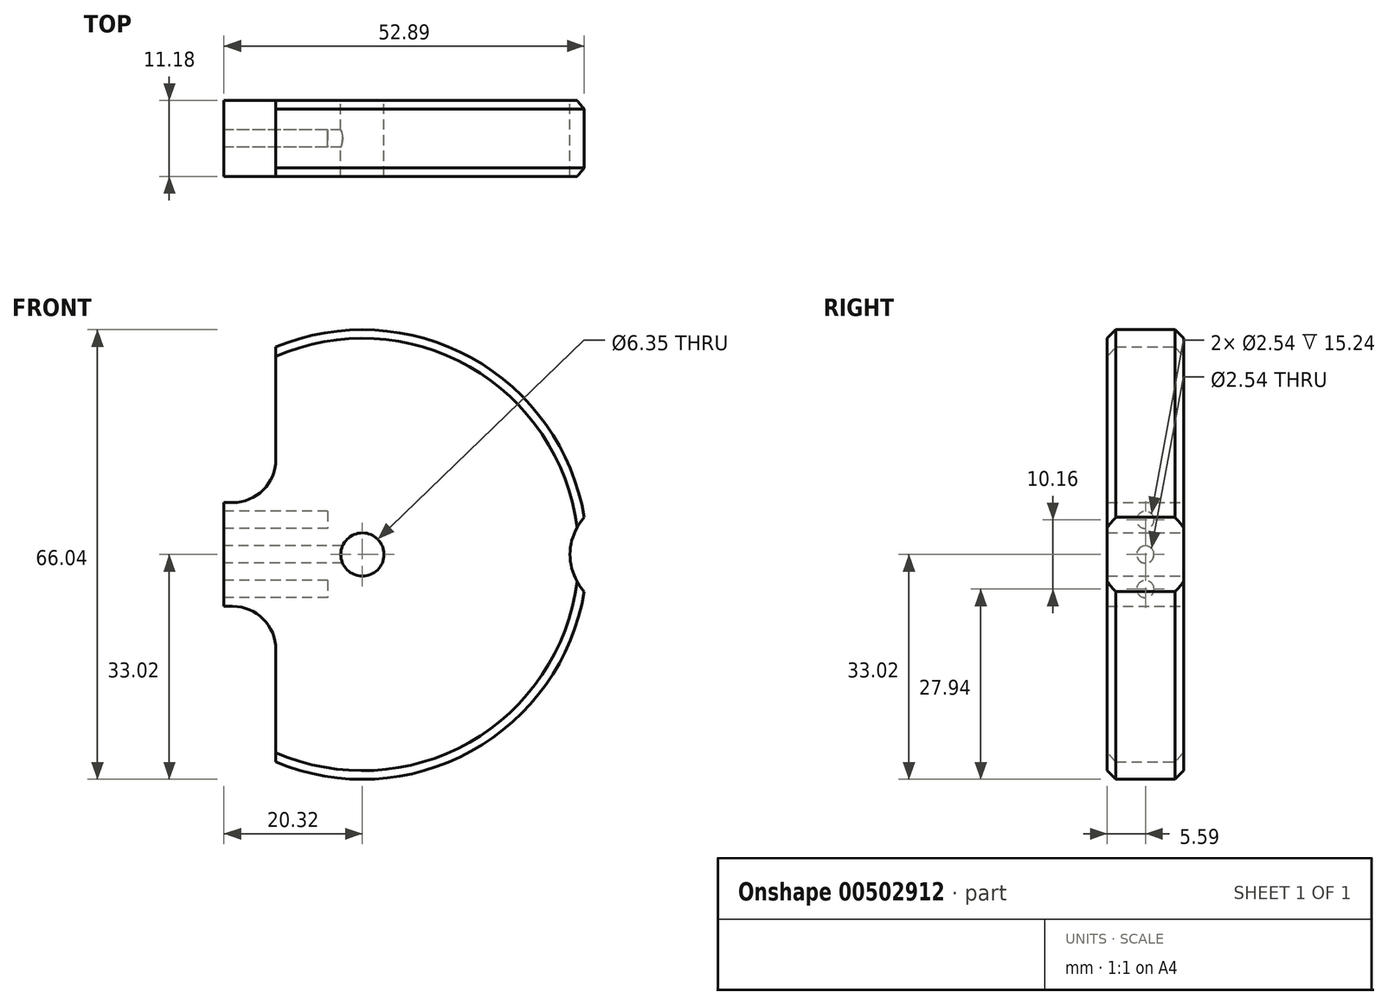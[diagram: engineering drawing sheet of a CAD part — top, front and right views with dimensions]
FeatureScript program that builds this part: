
annotation { "Feature Type Name" : "Feature", "Feature Type Description" : "" }
export const myFeature = defineFeature(function(context is Context, id is Id, definition is map)
    precondition{}
    {
        {
            var Q0;
            Q0=qCreatedBy(makeId("Front.planeOp"),FACE);
            var sketch = newSketch(context, id + "F0", { "sketchPlane" : qUnion([Q0])});
            skLineSegment(sketch, "E0", {"start": v(0, 0) * mm, "end": v(-82.35, 0) * mm, "construction": true});
            skLineSegment(sketch, "E1", {"start": v(-12.7, 30.48) * mm, "end": v(-12.7, 13.97) * mm});
            skLineSegment(sketch, "E2", {"start": v(-19.05, 7.62) * mm, "end": v(-20.32, 7.62) * mm});
            skLineSegment(sketch, "E3", {"start": v(-19.05, -7.62) * mm, "end": v(-20.32, -7.62) * mm});
            skLineSegment(sketch, "E4.trimOffspring", {"start": v(-20.32, 7.62) * mm, "end": v(-20.32, -7.62) * mm});
            skArc(sketch, "E5.trimOffspring", {"start": v(-12.7, -30.48) * mm, "mid": v(15.97, -28.9) * mm, "end": v(32.57, -5.46) * mm});
            skLineSegment(sketch, "E6.trimOffspring", {"start": v(-12.7, -13.97) * mm, "end": v(-12.7, -30.48) * mm});
            skCircle(sketch, "E7", {"center": v(0, 0) * mm, "radius": 3.18 * mm});
            skPoint(sketch, "E8.visualSharp", {"position": v(-12.7, 7.62) * mm});
            skArc(sketch, "E8.filletArc", {"start": v(-19.05, 7.62) * mm, "mid": v(-14.56, 9.48) * mm, "end": v(-12.7, 13.97) * mm});
            skPoint(sketch, "E9.visualSharp", {"position": v(-12.7, -7.62) * mm});
            skArc(sketch, "E9.filletArc", {"start": v(-12.7, -13.97) * mm, "mid": v(-14.56, -9.48) * mm, "end": v(-19.05, -7.62) * mm});
            skArc(sketch, "E10", {"start": v(32.57, 5.46) * mm, "mid": v(30.48, 0) * mm, "end": v(32.57, -5.46) * mm});
            skPoint(sketch, "E10.centerSnap0", {"position": v(33.02, 0) * mm});
            skArc(sketch, "E11.trimOffspring", {"start": v(32.57, 5.46) * mm, "mid": v(15.97, 28.9) * mm, "end": v(-12.7, 30.48) * mm});
            skSolve(sketch);
        }
        {
            var Q0;
            Q0 = qSketchRegion(id + "F0", true);
            extrude(context, id + "F1", {"entities" : qUnion([Q0]), "endBound" : BoundingType.SYMMETRIC, "depth" : 11.18 * mm});
        }
        {
            var Q0;
            Q0=makeQuery(id+"F1.opExtrude","SWEPT_FACE",FACE,{"disambiguationData":[OSD([sQuery(id+"F0.wireOp",EDGE,"E4.trimOffspring")])]});
            var sketch = newSketch(context, id + "F2", { "sketchPlane" : qUnion([Q0])});
            skCircle(sketch, "E12", {"center": v(0, 0) * mm, "radius": 1.27 * mm});
            skCircle(sketch, "E13", {"center": v(0, 5.08) * mm, "radius": 1.27 * mm});
            skCircle(sketch, "E14", {"center": v(0, -5.08) * mm, "radius": 1.27 * mm});
            skSolve(sketch);
        }
        {
            var Q0;
            Q0 = qSketchRegion(id + "F2", true);
            extrude(context, id + "F3", {"entities" : qUnion([Q0]), "operationType" : NewBodyOperationType.REMOVE, "oppositeDirection" : true, "depth" : 15.24 * mm});
        }
        {
            var Q0;
            Q0=makeQuery(id+"F2.imprint","IMPRINT",FACE,{"disambiguationData":[TD([[makeQuery(id+"F2.imprint","IMPRINT",EDGE,{"derivedFrom":sQuery(id+"F2.wireOp",EDGE,"E12")}),1.0]])]});
            extrude(context, id + "F4", {"entities" : qUnion([Q0]), "operationType" : NewBodyOperationType.REMOVE, "oppositeDirection" : true, "depth" : 19.05 * mm});
        }
        {
            var Q0;
            Q0=makeQuery(id+"F1.opExtrude","CAP_EDGE",EDGE,{"disambiguationData":[OSD([sQuery(id+"F0.wireOp",EDGE,"E11.trimOffspring")])],"isStart":false});
            var Q1;
            Q1=makeQuery(id+"F1.opExtrude","CAP_EDGE",EDGE,{"disambiguationData":[OSD([sQuery(id+"F0.wireOp",EDGE,"E5.trimOffspring")])],"isStart":false});
            var Q2;
            Q2=makeQuery(id+"F1.opExtrude","CAP_EDGE",EDGE,{"disambiguationData":[OSD([sQuery(id+"F0.wireOp",EDGE,"E11.trimOffspring")])],"isStart":true});
            var Q3;
            Q3=makeQuery(id+"F1.opExtrude","CAP_EDGE",EDGE,{"disambiguationData":[OSD([sQuery(id+"F0.wireOp",EDGE,"E5.trimOffspring")])],"isStart":true});
            chamfer(context, id + "F5", {"entities" : qUnion([Q0, Q1, Q2, Q3]), "width" : 1.27 * mm, "tangentPropagation" : true});
        }
    });
